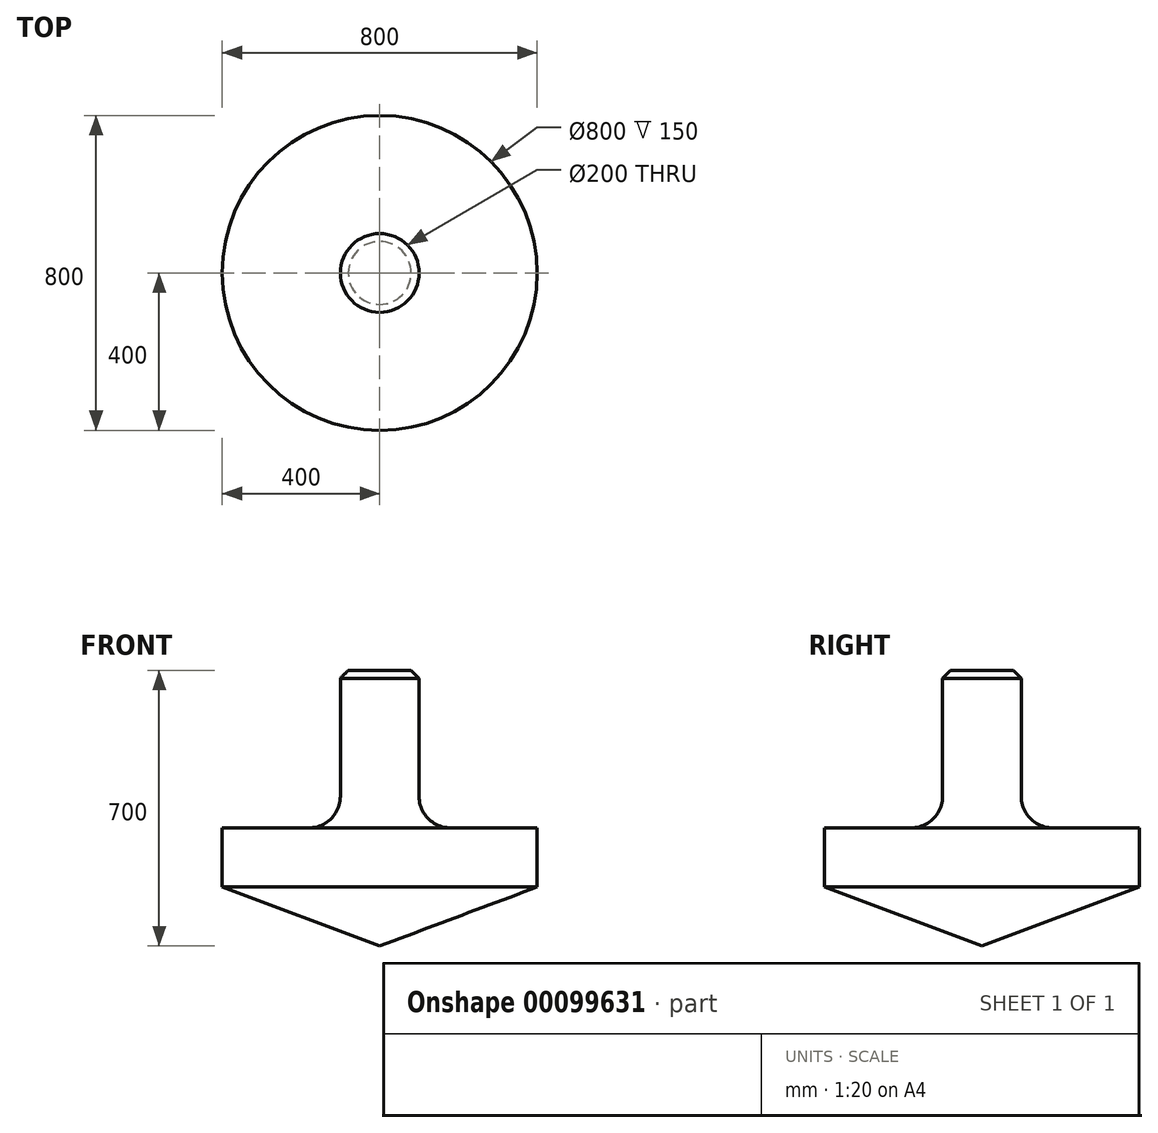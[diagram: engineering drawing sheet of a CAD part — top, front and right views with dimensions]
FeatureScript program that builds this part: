
annotation { "Feature Type Name" : "Feature", "Feature Type Description" : "" }
export const myFeature = defineFeature(function(context is Context, id is Id, definition is map)
    precondition{}
    {
        {
            var Q0;
            Q0=qCreatedBy(makeId("Front.planeOp"),FACE);
            var sketch = newSketch(context, id + "F0", { "sketchPlane" : qUnion([Q0])});
            skLineSegment(sketch, "E0", {"start": v(0, 0) * mm, "end": v(400, 150) * mm});
            skLineSegment(sketch, "E1", {"start": v(400, 150) * mm, "end": v(400, 300) * mm});
            skLineSegment(sketch, "E2", {"start": v(400, 300) * mm, "end": v(180, 300) * mm});
            skLineSegment(sketch, "E3", {"start": v(100, 380) * mm, "end": v(100, 700) * mm});
            skLineSegment(sketch, "E4", {"start": v(100, 700) * mm, "end": v(0, 700) * mm});
            skPoint(sketch, "E5.visualSharp", {"position": v(100, 300) * mm});
            skArc(sketch, "E5.filletArc", {"start": v(100, 380) * mm, "mid": v(123.43, 323.43) * mm, "end": v(180, 300) * mm});
            skLineSegment(sketch, "E6", {"start": v(0, -220.15) * mm, "end": v(0, 866.04) * mm, "construction": true});
            skSolve(sketch);
        }
        {
            var Q0;
            Q0 = qSketchRegion(id + "F0", true);
            var Q1;
            Q1 = qConstructionFilter(qBodyType(qCreatedBy(id + "F0" ,EDGE), BodyType.WIRE), ConstructionObject.NO);
            var Q2;
            Q2=sQuery(id+"F0.wireOp",EDGE,"E6");
            revolve(context, id + "F1", {"bodyType" : ToolBodyType.SURFACE, "entities" : qUnion([Q0]), "surfaceEntities" : qUnion([Q1]), "axis" : qUnion([Q2]), "revolveType" : RevolveType.FULL});
        }
        {
            var Q0;
            Q0=makeQuery(id+"F1.opRevolve","SWEPT_EDGE",EDGE,{"disambiguationData":[OSD([sQuery(id+"F0.wireOp",VERTEX,"E4.start")])]});
            chamfer(context, id + "F2", {"entities" : qUnion([Q0]), "width" : 20 * mm, "tangentPropagation" : true});
        }
    });
